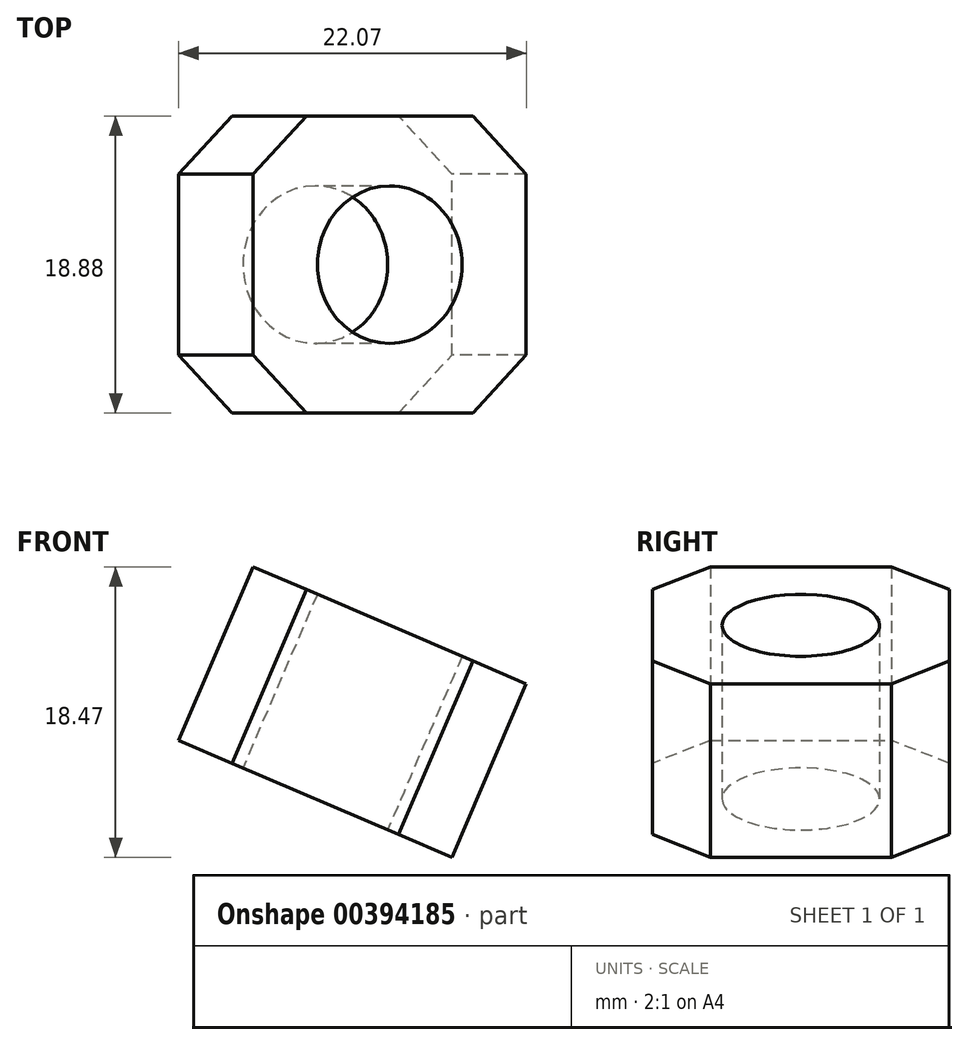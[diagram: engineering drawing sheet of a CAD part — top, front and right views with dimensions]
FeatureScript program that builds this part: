
annotation { "Feature Type Name" : "Feature", "Feature Type Description" : "" }
export const myFeature = defineFeature(function(context is Context, id is Id, definition is map)
    precondition{}
    {
        {
            var Q0;
            Q0=qCreatedBy(makeId("Front.planeOp"),FACE);
            var sketch = newSketch(context, id + "F0", { "sketchPlane" : qUnion([Q0])});
            skLineSegment(sketch, "E0", {"start": v(0, 0) * mm, "end": v(-70, 0) * mm});
            skLineSegment(sketch, "E1", {"start": v(-70, 0) * mm, "end": v(-70, 30) * mm});
            skLineSegment(sketch, "E2", {"start": v(-70, 30) * mm, "end": v(0, 0) * mm});
            skLineSegment(sketch, "E3", {"start": v(0, 0) * mm, "end": v(1200, 0) * mm});
            skLineSegment(sketch, "E4", {"start": v(1200, 0) * mm, "end": v(1200, 1400) * mm});
            skLineSegment(sketch, "E5", {"start": v(1200, 1400) * mm, "end": v(0, 0) * mm});
            skSolve(sketch);
        }
        {
            var Q0;
            Q0=qCreatedBy(makeId("Top.planeOp"),FACE);
            var sketch = newSketch(context, id + "F1", { "sketchPlane" : qUnion([Q0])});
            skLineSegment(sketch, "E6", {"start": v(0, 0) * mm, "end": v(0, -500) * mm, "construction": true});
            skLineSegment(sketch, "E7", {"start": v(0, 0) * mm, "end": v(0, 500) * mm, "construction": true});
            skSolve(sketch);
        }
        {
            var Q0;
            Q0=sQuery(id+"F1.wireOp",EDGE,"E6");
            cPoint(context, id + "F2", {"entities" : qUnion([Q0]), "parameter" : 0.5});
        }
        {
            var Q0;
            Q0=sQuery(id+"F0.wireOp",VERTEX,"E2.start");
            var Q1;
            Q1=sQuery(id+"F1.wireOp",VERTEX,"E7.start");
            var Q2;
            Q2 = qCreatedBy(id + "F2" ,VERTEX);
            cPlane(context, id + "F3", {"entities" : qUnion([Q0, Q1, Q2]), "cplaneType" : CPlaneType.THREE_POINT, "offset" : 25 * mm, "width" : 150 * mm, "height" : 150 * mm});
        }
        {
            var Q0;
            Q0=qCreatedBy(id+"F3.planeOp",FACE);
            var sketch = newSketch(context, id + "F4", { "sketchPlane" : qUnion([Q0])});
            skCircle(sketch, "E8", {"center": v(0, 0) * mm, "radius": 5 * mm});
            skLineSegment(sketch, "E9.bottom", {"start": v(-9.43, 9.44) * mm, "end": v(9.44, 9.44) * mm, "construction": true});
            skLineSegment(sketch, "E9.top", {"start": v(-9.44, -9.44) * mm, "end": v(9.43, -9.44) * mm, "construction": true});
            skLineSegment(sketch, "E9.right", {"start": v(9.44, 9.44) * mm, "end": v(9.43, -9.44) * mm, "construction": true});
            skLineSegment(sketch, "E10", {"start": v(0, 9.44) * mm, "end": v(-5.75, 9.44) * mm});
            skLineSegment(sketch, "E11", {"start": v(0, 9.44) * mm, "end": v(5.75, 9.44) * mm});
            skLineSegment(sketch, "E12", {"start": v(-9.44, -9.44) * mm, "end": v(9.44, 9.44) * mm, "construction": true});
            skLineSegment(sketch, "E13", {"start": v(-9.43, 9.44) * mm, "end": v(-9.44, -9.44) * mm, "construction": true});
            skLineSegment(sketch, "E14", {"start": v(-5.75, 9.44) * mm, "end": v(-9.44, 5.75) * mm});
            skLineSegment(sketch, "E15", {"start": v(-9.43, 0) * mm, "end": v(-9.43, 5.75) * mm});
            skLineSegment(sketch, "E16", {"start": v(-9.43, 0) * mm, "end": v(-9.44, -5.75) * mm});
            skLineSegment(sketch, "E17", {"start": v(-9.44, -5.75) * mm, "end": v(-5.75, -9.44) * mm});
            skLineSegment(sketch, "E18", {"start": v(-5.75, -9.44) * mm, "end": v(0, -9.44) * mm});
            skLineSegment(sketch, "E19", {"start": v(0, -9.44) * mm, "end": v(5.75, -9.44) * mm});
            skLineSegment(sketch, "E20", {"start": v(5.75, -9.44) * mm, "end": v(9.44, -5.75) * mm});
            skLineSegment(sketch, "E21", {"start": v(9.44, -5.75) * mm, "end": v(9.44, 5.75) * mm});
            skLineSegment(sketch, "E22", {"start": v(9.44, 5.75) * mm, "end": v(5.75, 9.44) * mm});
            skSolve(sketch);
        }
        {
            var Q0;
            Q0=makeQuery(id+"F4.imprint","IMPRINT",FACE,{"disambiguationData":[TD([[makeQuery(id+"F4.imprint","IMPRINT",EDGE,{"derivedFrom":sQuery(id+"F4.wireOp",EDGE,"E8")}),-1.0]])]});
            extrude(context, id + "F5", {"entities" : qUnion([Q0]), "depth" : 12 * mm});
        }
    });
